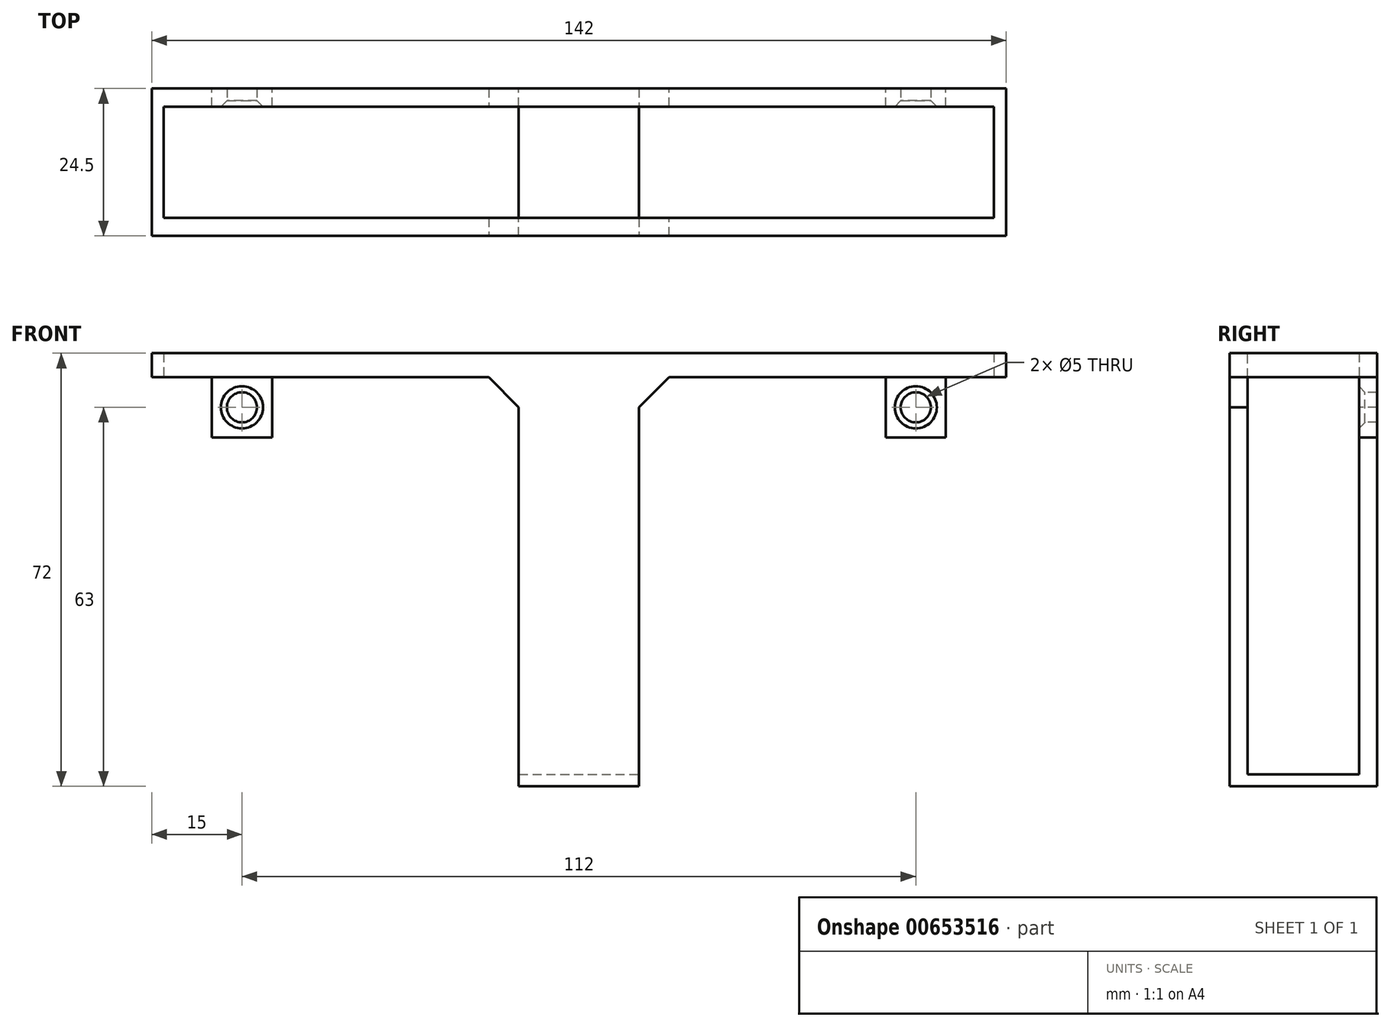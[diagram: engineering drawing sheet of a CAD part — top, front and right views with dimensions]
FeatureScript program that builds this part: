
annotation { "Feature Type Name" : "Feature", "Feature Type Description" : "" }
export const myFeature = defineFeature(function(context is Context, id is Id, definition is map)
    precondition{}
    {
        {
            var Q0;
            Q0=qCreatedBy(makeId("Top.planeOp"),FACE);
            var sketch = newSketch(context, id + "F0", { "sketchPlane" : qUnion([Q0])});
            skLineSegment(sketch, "E0.bottom", {"start": v(10, -12.25) * mm, "end": v(-10, -12.25) * mm});
            skLineSegment(sketch, "E0.top", {"start": v(10, 12.25) * mm, "end": v(-10, 12.25) * mm});
            skLineSegment(sketch, "E0.left", {"start": v(10, -12.25) * mm, "end": v(10, 12.25) * mm});
            skLineSegment(sketch, "E0.right", {"start": v(-10, -12.25) * mm, "end": v(-10, 12.25) * mm});
            skPoint(sketch, "E0.middle", {"position": v(0, 0) * mm});
            skSolve(sketch);
        }
        {
            var Q0;
            Q0 = qSketchRegion(id + "F0", true);
            extrude(context, id + "F1", {"entities" : qUnion([Q0]), "depth" : 2 * mm, "offsetDistance" : 25 * mm});
        }
        {
            var Q0;
            Q0=makeQuery(id+"F1.opExtrude","CAP_FACE",FACE,{"disambiguationData":[OSD([sQuery(id+"F0.wireOp",EDGE,"E0.bottom"),sQuery(id+"F0.wireOp",EDGE,"E0.top"),sQuery(id+"F0.wireOp",EDGE,"E0.left"),sQuery(id+"F0.wireOp",EDGE,"E0.right")])],"isStart":false});
            var sketch = newSketch(context, id + "F2", { "sketchPlane" : qUnion([Q0])});
            skLineSegment(sketch, "E1.bottom", {"start": v(-10, 12.25) * mm, "end": v(10, 12.25) * mm});
            skLineSegment(sketch, "E1.top", {"start": v(-10, 9.25) * mm, "end": v(10, 9.25) * mm});
            skLineSegment(sketch, "E1.left", {"start": v(-10, 12.25) * mm, "end": v(-10, 9.25) * mm});
            skLineSegment(sketch, "E1.right", {"start": v(10, 12.25) * mm, "end": v(10, 9.25) * mm});
            skLineSegment(sketch, "E2.bottom", {"start": v(-10, -12.25) * mm, "end": v(10, -12.25) * mm});
            skLineSegment(sketch, "E2.top", {"start": v(-10, -9.25) * mm, "end": v(10, -9.25) * mm});
            skLineSegment(sketch, "E2.left", {"start": v(-10, -12.25) * mm, "end": v(-10, -9.25) * mm});
            skLineSegment(sketch, "E2.right", {"start": v(10, -12.25) * mm, "end": v(10, -9.25) * mm});
            skSolve(sketch);
        }
        {
            var Q0;
            Q0=makeQuery(id+"F2.imprint","IMPRINT",FACE,{"disambiguationData":[TD([[makeQuery(id+"F2.imprint","IMPRINT",EDGE,{"derivedFrom":sQuery(id+"F2.wireOp",EDGE,"E1.bottom")}),1.0]])]});
            var Q1;
            Q1=makeQuery(id+"F2.imprint","IMPRINT",FACE,{"disambiguationData":[TD([[makeQuery(id+"F2.imprint","IMPRINT",EDGE,{"derivedFrom":sQuery(id+"F2.wireOp",EDGE,"E2.bottom")}),-1.0]])]});
            extrude(context, id + "F3", {"entities" : qUnion([Q0, Q1]), "operationType" : NewBodyOperationType.ADD, "depth" : 70 * mm, "offsetDistance" : 25 * mm});
        }
        {
            var Q0;
            Q0=makeQuery(id+"F3.boolean.opBoolean","MERGE",FACE,{"derivedFrom":[makeQuery(id+"F1.opExtrude","SWEPT_FACE",FACE,{"disambiguationData":[OSD([sQuery(id+"F0.wireOp",EDGE,"E0.bottom")])]}),makeQuery(id+"F3.opExtrude","SWEPT_FACE",FACE,{"disambiguationData":[OSD([sQuery(id+"F2.wireOp",EDGE,"E2.bottom")])]})]});
            var sketch = newSketch(context, id + "F4", { "sketchPlane" : qUnion([Q0])});
            skLineSegment(sketch, "E3.bottom", {"start": v(0, 72) * mm, "end": v(71, 72) * mm});
            skLineSegment(sketch, "E3.top", {"start": v(0, 68) * mm, "end": v(71, 68) * mm});
            skLineSegment(sketch, "E3.left", {"start": v(0, 72) * mm, "end": v(0, 68) * mm});
            skLineSegment(sketch, "E3.right", {"start": v(71, 72) * mm, "end": v(71, 68) * mm});
            skLineSegment(sketch, "E4.bottom", {"start": v(0, 68) * mm, "end": v(-71, 68) * mm});
            skLineSegment(sketch, "E4.top", {"start": v(0, 72) * mm, "end": v(-71, 72) * mm});
            skLineSegment(sketch, "E4.left", {"start": v(0, 68) * mm, "end": v(0, 72) * mm});
            skLineSegment(sketch, "E4.right", {"start": v(-71, 68) * mm, "end": v(-71, 72) * mm});
            skSolve(sketch);
        }
        {
            var Q0;
            Q0 = qSketchRegion(id + "F4", true);
            var Q1;
            Q1=makeQuery(id+"F3.opExtrude","SWEPT_FACE",FACE,{"disambiguationData":[OSD([sQuery(id+"F2.wireOp",EDGE,"E2.top")])]});
            extrude(context, id + "F5", {"entities" : qUnion([Q0]), "operationType" : NewBodyOperationType.ADD, "endBound" : BoundingType.UP_TO_SURFACE, "oppositeDirection" : true, "depth" : 25 * mm, "endBoundEntityFace" : qUnion([Q1]), "offsetDistance" : 25 * mm});
        }
        {
            var Q0;
            Q0=makeQuery(id+"F3.opExtrude","SWEPT_FACE",FACE,{"disambiguationData":[OSD([sQuery(id+"F2.wireOp",EDGE,"E1.top")])]});
            var sketch = newSketch(context, id + "F6", { "sketchPlane" : qUnion([Q0])});
            skLineSegment(sketch, "E5.bottom", {"start": v(0, 72) * mm, "end": v(-71, 72) * mm});
            skLineSegment(sketch, "E5.top", {"start": v(0, 68) * mm, "end": v(-71, 68) * mm});
            skLineSegment(sketch, "E5.left", {"start": v(0, 72) * mm, "end": v(0, 68) * mm});
            skLineSegment(sketch, "E5.right", {"start": v(-71, 72) * mm, "end": v(-71, 68) * mm});
            skLineSegment(sketch, "E6.bottom", {"start": v(0, 72) * mm, "end": v(71, 72) * mm});
            skLineSegment(sketch, "E6.top", {"start": v(0, 68) * mm, "end": v(71, 68) * mm});
            skLineSegment(sketch, "E6.right", {"start": v(71, 72) * mm, "end": v(71, 68) * mm});
            skSolve(sketch);
        }
        {
            var Q0;
            Q0 = qSketchRegion(id + "F6", true);
            var Q1;
            Q1=makeQuery(id+"F3.boolean.opBoolean","MERGE",FACE,{"derivedFrom":[makeQuery(id+"F1.opExtrude","SWEPT_FACE",FACE,{"disambiguationData":[OSD([sQuery(id+"F0.wireOp",EDGE,"E0.top")])]}),makeQuery(id+"F3.opExtrude","SWEPT_FACE",FACE,{"disambiguationData":[OSD([sQuery(id+"F2.wireOp",EDGE,"E1.bottom")])]})]});
            extrude(context, id + "F7", {"entities" : qUnion([Q0]), "operationType" : NewBodyOperationType.ADD, "endBound" : BoundingType.UP_TO_SURFACE, "oppositeDirection" : true, "depth" : 25 * mm, "endBoundEntityFace" : qUnion([Q1]), "offsetDistance" : 25 * mm});
        }
        {
            var Q0;
            Q0=makeQuery(id+"F7.boolean.opBoolean","MERGE",FACE,{"derivedFrom":[makeQuery(id+"F3.opExtrude","SWEPT_FACE",FACE,{"disambiguationData":[OSD([sQuery(id+"F2.wireOp",EDGE,"E1.top")])]}),makeQuery(id+"F7.opExtrude","CAP_FACE",FACE,{"disambiguationData":[OSD([sQuery(id+"F6.wireOp",EDGE,"E5.bottom"),sQuery(id+"F6.wireOp",EDGE,"E5.top"),sQuery(id+"F6.wireOp",EDGE,"E5.right"),sQuery(id+"F6.wireOp",EDGE,"E6.bottom"),sQuery(id+"F6.wireOp",EDGE,"E6.top"),sQuery(id+"F6.wireOp",EDGE,"E6.right")])],"isStart":true})]});
            var sketch = newSketch(context, id + "F8", { "sketchPlane" : qUnion([Q0])});
            skLineSegment(sketch, "E7.bottom", {"start": v(-71, 72) * mm, "end": v(-69, 72) * mm});
            skLineSegment(sketch, "E7.top", {"start": v(-71, 68) * mm, "end": v(-69, 68) * mm});
            skLineSegment(sketch, "E7.left", {"start": v(-71, 72) * mm, "end": v(-71, 68) * mm});
            skLineSegment(sketch, "E7.right", {"start": v(-69, 72) * mm, "end": v(-69, 68) * mm});
            skLineSegment(sketch, "E8.bottom", {"start": v(71, 72) * mm, "end": v(69, 72) * mm});
            skLineSegment(sketch, "E8.top", {"start": v(71, 68) * mm, "end": v(69, 68) * mm});
            skLineSegment(sketch, "E8.left", {"start": v(71, 72) * mm, "end": v(71, 68) * mm});
            skLineSegment(sketch, "E8.right", {"start": v(69, 72) * mm, "end": v(69, 68) * mm});
            skSolve(sketch);
        }
        {
            var Q0;
            Q0 = qSketchRegion(id + "F8", true);
            var Q1;
            {var subQ0=sQuery(id+"F2.wireOp",EDGE,"E2.top");Q1=makeQuery(id+"F5.boolean.opBoolean","MERGE",FACE,{"derivedFrom":[makeQuery(id+"F3.opExtrude","SWEPT_FACE",FACE,{"disambiguationData":[OSD([subQ0])]}),makeQuery(id+"F5.opExtrude","CAP_FACE",FACE,{"disambiguationData":[OSD([subQ0])],"isStart":false})]});}
            extrude(context, id + "F9", {"entities" : qUnion([Q0]), "operationType" : NewBodyOperationType.ADD, "endBound" : BoundingType.UP_TO_SURFACE, "depth" : 25 * mm, "endBoundEntityFace" : qUnion([Q1]), "offsetDistance" : 25 * mm});
        }
        {
            var Q0;
            Q0=makeQuery(id+"F7.boolean.opBoolean","INTERSECT",EDGE,{"derivedFrom":[makeQuery(id+"F3.boolean.opBoolean","MERGE",FACE,{"derivedFrom":[makeQuery(id+"F1.opExtrude","SWEPT_FACE",FACE,{"disambiguationData":[OSD([sQuery(id+"F0.wireOp",EDGE,"E0.left")])]}),makeQuery(id+"F3.opExtrude","SWEPT_FACE",FACE,{"disambiguationData":[OSD([sQuery(id+"F2.wireOp",EDGE,"E1.right")])]}),makeQuery(id+"F3.opExtrude","SWEPT_FACE",FACE,{"disambiguationData":[OSD([sQuery(id+"F2.wireOp",EDGE,"E2.right")])]})]}),makeQuery(id+"F7.opExtrude","SWEPT_FACE",FACE,{"disambiguationData":[OSD([sQuery(id+"F6.wireOp",EDGE,"E5.top"),sQuery(id+"F6.wireOp",EDGE,"E6.top")])]})]});
            var Q1;
            Q1=makeQuery(id+"F5.boolean.opBoolean","INTERSECT",EDGE,{"derivedFrom":[makeQuery(id+"F3.boolean.opBoolean","MERGE",FACE,{"derivedFrom":[makeQuery(id+"F1.opExtrude","SWEPT_FACE",FACE,{"disambiguationData":[OSD([sQuery(id+"F0.wireOp",EDGE,"E0.left")])]}),makeQuery(id+"F3.opExtrude","SWEPT_FACE",FACE,{"disambiguationData":[OSD([sQuery(id+"F2.wireOp",EDGE,"E1.right")])]}),makeQuery(id+"F3.opExtrude","SWEPT_FACE",FACE,{"disambiguationData":[OSD([sQuery(id+"F2.wireOp",EDGE,"E2.right")])]})]}),makeQuery(id+"F5.opExtrude","SWEPT_FACE",FACE,{"disambiguationData":[OSD([sQuery(id+"F4.wireOp",EDGE,"E3.top"),sQuery(id+"F4.wireOp",EDGE,"E4.bottom")])]})]});
            var Q2;
            Q2=makeQuery(id+"F7.boolean.opBoolean","INTERSECT",EDGE,{"derivedFrom":[makeQuery(id+"F3.boolean.opBoolean","MERGE",FACE,{"derivedFrom":[makeQuery(id+"F1.opExtrude","SWEPT_FACE",FACE,{"disambiguationData":[OSD([sQuery(id+"F0.wireOp",EDGE,"E0.right")])]}),makeQuery(id+"F3.opExtrude","SWEPT_FACE",FACE,{"disambiguationData":[OSD([sQuery(id+"F2.wireOp",EDGE,"E1.left")])]}),makeQuery(id+"F3.opExtrude","SWEPT_FACE",FACE,{"disambiguationData":[OSD([sQuery(id+"F2.wireOp",EDGE,"E2.left")])]})]}),makeQuery(id+"F7.opExtrude","SWEPT_FACE",FACE,{"disambiguationData":[OSD([sQuery(id+"F6.wireOp",EDGE,"E5.top"),sQuery(id+"F6.wireOp",EDGE,"E6.top")])]})]});
            var Q3;
            Q3=makeQuery(id+"F5.boolean.opBoolean","INTERSECT",EDGE,{"derivedFrom":[makeQuery(id+"F3.boolean.opBoolean","MERGE",FACE,{"derivedFrom":[makeQuery(id+"F1.opExtrude","SWEPT_FACE",FACE,{"disambiguationData":[OSD([sQuery(id+"F0.wireOp",EDGE,"E0.right")])]}),makeQuery(id+"F3.opExtrude","SWEPT_FACE",FACE,{"disambiguationData":[OSD([sQuery(id+"F2.wireOp",EDGE,"E1.left")])]}),makeQuery(id+"F3.opExtrude","SWEPT_FACE",FACE,{"disambiguationData":[OSD([sQuery(id+"F2.wireOp",EDGE,"E2.left")])]})]}),makeQuery(id+"F5.opExtrude","SWEPT_FACE",FACE,{"disambiguationData":[OSD([sQuery(id+"F4.wireOp",EDGE,"E3.top"),sQuery(id+"F4.wireOp",EDGE,"E4.bottom")])]})]});
            chamfer(context, id + "F10", {"entities" : qUnion([Q0, Q1, Q2, Q3]), "width" : 5 * mm, "tangentPropagation" : true});
        }
        {
            var Q0;
            {var subQ0=sQuery(id+"F2.wireOp",EDGE,"E1.bottom");var subQ1=sQuery(id+"F0.wireOp",EDGE,"E0.top");Q0=makeQuery(id+"F7.boolean.opBoolean","MERGE",FACE,{"derivedFrom":[makeQuery(id+"F3.boolean.opBoolean","MERGE",FACE,{"derivedFrom":[makeQuery(id+"F1.opExtrude","SWEPT_FACE",FACE,{"disambiguationData":[OSD([subQ1])]}),makeQuery(id+"F3.opExtrude","SWEPT_FACE",FACE,{"disambiguationData":[OSD([subQ0])]})]}),makeQuery(id+"F7.opExtrude","CAP_FACE",FACE,{"disambiguationData":[OSD([subQ1,subQ0])],"isStart":false})]});}
            var sketch = newSketch(context, id + "F11", { "sketchPlane" : qUnion([Q0])});
            skLineSegment(sketch, "E9.bottom", {"start": v(-71, 68) * mm, "end": v(-61, 68) * mm});
            skLineSegment(sketch, "E9.top", {"start": v(-71, 58) * mm, "end": v(-61, 58) * mm});
            skLineSegment(sketch, "E9.left", {"start": v(-71, 68) * mm, "end": v(-71, 58) * mm});
            skLineSegment(sketch, "E9.right", {"start": v(-61, 68) * mm, "end": v(-61, 58) * mm});
            skLineSegment(sketch, "E10.bottom", {"start": v(-61, 58) * mm, "end": v(-51, 58) * mm});
            skLineSegment(sketch, "E10.top", {"start": v(-61, 68) * mm, "end": v(-51, 68) * mm});
            skLineSegment(sketch, "E10.left", {"start": v(-61, 58) * mm, "end": v(-61, 68) * mm});
            skLineSegment(sketch, "E10.right", {"start": v(-51, 58) * mm, "end": v(-51, 68) * mm});
            skLineSegment(sketch, "E11.bottom", {"start": v(71, 68) * mm, "end": v(61, 68) * mm});
            skLineSegment(sketch, "E11.top", {"start": v(71, 58) * mm, "end": v(61, 58) * mm});
            skLineSegment(sketch, "E11.left", {"start": v(71, 68) * mm, "end": v(71, 58) * mm});
            skLineSegment(sketch, "E11.right", {"start": v(61, 68) * mm, "end": v(61, 58) * mm});
            skLineSegment(sketch, "E12.bottom", {"start": v(61, 68) * mm, "end": v(51, 68) * mm});
            skLineSegment(sketch, "E12.top", {"start": v(61, 58) * mm, "end": v(51, 58) * mm});
            skLineSegment(sketch, "E12.right", {"start": v(51, 68) * mm, "end": v(51, 58) * mm});
            skSolve(sketch);
        }
        {
            var Q0;
            Q0=makeQuery(id+"F11.imprint","IMPRINT",FACE,{"disambiguationData":[TD([[makeQuery(id+"F11.imprint","IMPRINT",EDGE,{"derivedFrom":sQuery(id+"F11.wireOp",EDGE,"E10.bottom")}),1.0]])]});
            var Q1;
            Q1=makeQuery(id+"F11.imprint","IMPRINT",FACE,{"disambiguationData":[TD([[makeQuery(id+"F11.imprint","IMPRINT",EDGE,{"derivedFrom":sQuery(id+"F11.wireOp",EDGE,"E12.bottom")}),1.0]])]});
            var Q2;
            Q2=makeQuery(id+"F7.boolean.opBoolean","MERGE",FACE,{"derivedFrom":[makeQuery(id+"F3.opExtrude","SWEPT_FACE",FACE,{"disambiguationData":[OSD([sQuery(id+"F2.wireOp",EDGE,"E1.top")])]}),makeQuery(id+"F7.opExtrude","CAP_FACE",FACE,{"disambiguationData":[OSD([sQuery(id+"F6.wireOp",EDGE,"E5.bottom"),sQuery(id+"F6.wireOp",EDGE,"E5.top"),sQuery(id+"F6.wireOp",EDGE,"E5.right"),sQuery(id+"F6.wireOp",EDGE,"E6.bottom"),sQuery(id+"F6.wireOp",EDGE,"E6.top"),sQuery(id+"F6.wireOp",EDGE,"E6.right")])],"isStart":true})]});
            extrude(context, id + "F12", {"entities" : qUnion([Q0, Q1]), "operationType" : NewBodyOperationType.ADD, "endBound" : BoundingType.UP_TO_SURFACE, "oppositeDirection" : true, "depth" : 25 * mm, "endBoundEntityFace" : qUnion([Q2]), "offsetDistance" : 25 * mm});
        }
        {
            var Q0;
            {var subQ0=sQuery(id+"F6.wireOp",EDGE,"E6.right");var subQ1=sQuery(id+"F6.wireOp",EDGE,"E6.top");var subQ2=sQuery(id+"F6.wireOp",EDGE,"E6.bottom");var subQ3=sQuery(id+"F6.wireOp",EDGE,"E5.right");var subQ4=sQuery(id+"F6.wireOp",EDGE,"E5.top");var subQ5=sQuery(id+"F6.wireOp",EDGE,"E5.bottom");var subQ6=sQuery(id+"F2.wireOp",EDGE,"E1.top");Q0=makeQuery(id+"F12.boolean.opBoolean","MERGE",FACE,{"derivedFrom":[makeQuery(id+"F7.boolean.opBoolean","MERGE",FACE,{"derivedFrom":[makeQuery(id+"F3.opExtrude","SWEPT_FACE",FACE,{"disambiguationData":[OSD([subQ6])]}),makeQuery(id+"F7.opExtrude","CAP_FACE",FACE,{"disambiguationData":[OSD([subQ5,subQ4,subQ3,subQ2,subQ1,subQ0])],"isStart":true})]}),makeQuery(id+"F12.opExtrude","CAP_FACE",FACE,{"disambiguationData":[OSD([subQ6,subQ5,subQ4,subQ3,subQ2,subQ1,subQ0]),OD(0.0)],"isStart":false}),makeQuery(id+"F12.opExtrude","CAP_FACE",FACE,{"disambiguationData":[OSD([subQ6,subQ5,subQ4,subQ3,subQ2,subQ1,subQ0]),OD(1.0)],"isStart":false})]});}
            var sketch = newSketch(context, id + "F13", { "sketchPlane" : qUnion([Q0])});
            skLineSegment(sketch, "E13", {"start": v(-61, 68) * mm, "end": v(-51, 58) * mm});
            skLineSegment(sketch, "E14", {"start": v(-51, 58) * mm, "end": v(-51, 68) * mm});
            skLineSegment(sketch, "E15", {"start": v(-51, 68) * mm, "end": v(-61, 58) * mm});
            skPoint(sketch, "E16", {"position": v(-56, 63) * mm});
            skLineSegment(sketch, "E17", {"start": v(51, 68) * mm, "end": v(61, 58) * mm});
            skLineSegment(sketch, "E18", {"start": v(61, 58) * mm, "end": v(61, 68) * mm});
            skLineSegment(sketch, "E19", {"start": v(61, 68) * mm, "end": v(51, 58) * mm});
            skPoint(sketch, "E20", {"position": v(56, 63) * mm});
            skSolve(sketch);
        }
        {
            var Q0;
            Q0=sQuery(id+"F13.wireOp",VERTEX,"E20");
            var Q1;
            Q1=sQuery(id+"F13.wireOp",VERTEX,"E16");
            var Q2;
            Q2=makeQuery(id+"F1.opExtrude","SWEPT_BODY",BODY,{"disambiguationData":[OSD([sQuery(id+"F0.wireOp",EDGE,"E0.bottom"),sQuery(id+"F0.wireOp",EDGE,"E0.top"),sQuery(id+"F0.wireOp",EDGE,"E0.left"),sQuery(id+"F0.wireOp",EDGE,"E0.right")])]});
            hole(context, id + "F14", {"style" : HoleStyle.C_SINK, "endStyle" : HoleEndStyle.THROUGH, "holeDiameter" : 5 * mm, "cSinkDiameter" : 7 * mm, "cSinkAngle" : 90 * degree, "majorDiameter" : 5 * mm, "isTappedThrough" : true, "tappedDepth" : 12 * mm, "tapClearance" : 3, "locations" : qUnion([Q0, Q1]), "scope" : qUnion([Q2])});
        }
    });
